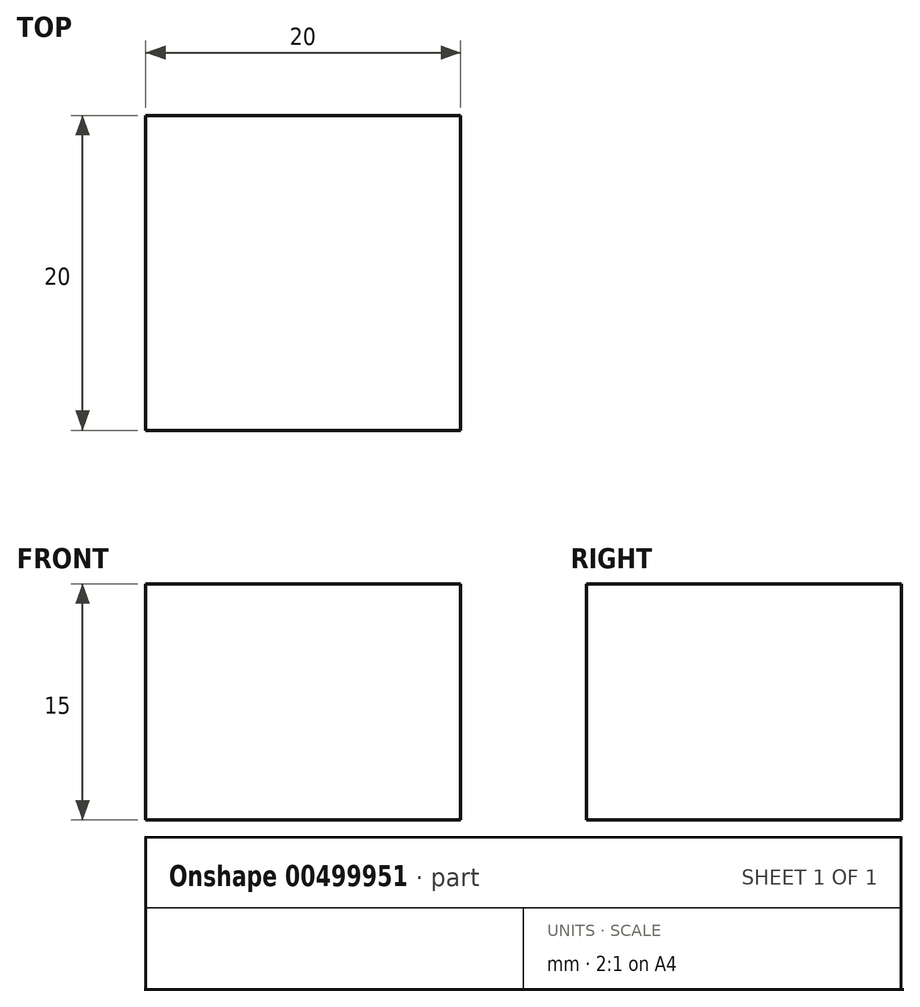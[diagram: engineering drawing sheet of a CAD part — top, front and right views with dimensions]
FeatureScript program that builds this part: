
annotation { "Feature Type Name" : "Feature", "Feature Type Description" : "" }
export const myFeature = defineFeature(function(context is Context, id is Id, definition is map)
    precondition{}
    {
        {
            var Q0;
            Q0=qCreatedBy(makeId("Top.planeOp"),FACE);
            var sketch = newSketch(context, id + "F0", { "sketchPlane" : qUnion([Q0])});
            skLineSegment(sketch, "E0.bottom", {"start": v(-7.52, 3.42) * mm, "end": v(12.48, 3.42) * mm});
            skLineSegment(sketch, "E0.top", {"start": v(-7.52, -16.58) * mm, "end": v(12.48, -16.58) * mm});
            skLineSegment(sketch, "E0.left", {"start": v(-7.52, 3.42) * mm, "end": v(-7.52, -16.58) * mm});
            skLineSegment(sketch, "E0.right", {"start": v(12.48, 3.42) * mm, "end": v(12.48, -16.58) * mm});
            skSolve(sketch);
        }
        {
            var Q0;
            Q0 = qSketchRegion(id + "F0", true);
            extrude(context, id + "F1", {"entities" : qUnion([Q0]), "depth" : 15 * mm});
        }
    });
